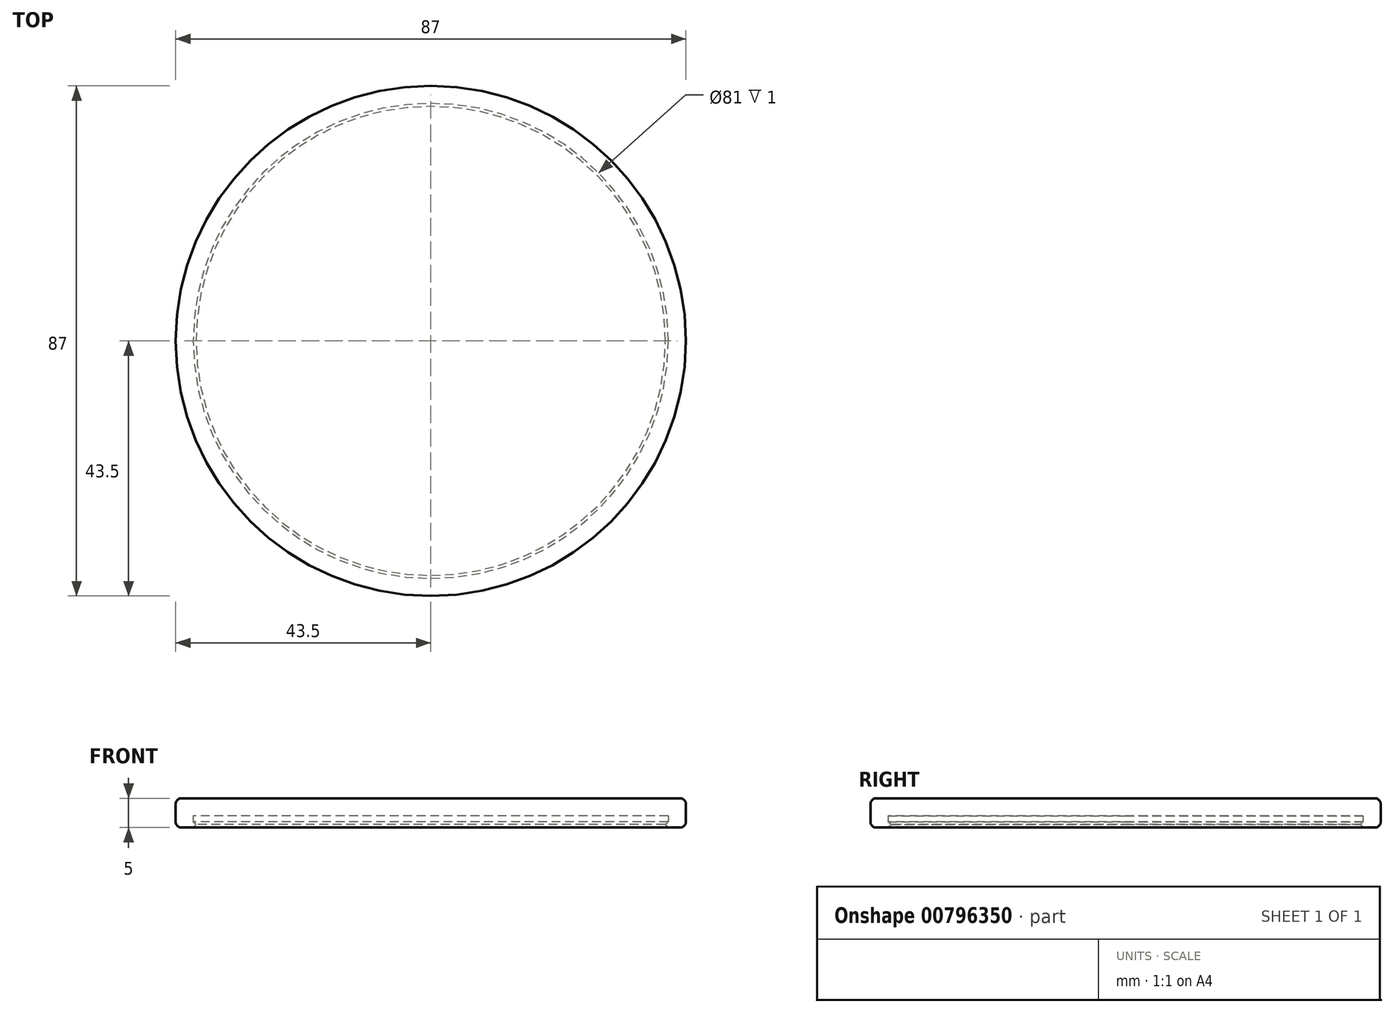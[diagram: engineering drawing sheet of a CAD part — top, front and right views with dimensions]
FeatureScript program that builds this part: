
annotation { "Feature Type Name" : "Feature", "Feature Type Description" : "" }
export const myFeature = defineFeature(function(context is Context, id is Id, definition is map)
    precondition{}
    {
        {
            var Q0;
            Q0=qCreatedBy(makeId("Top.planeOp"),FACE);
            var sketch = newSketch(context, id + "F0", { "sketchPlane" : qUnion([Q0])});
            skCircle(sketch, "E0", {"center": v(0, 0) * mm, "radius": 40.5 * mm});
            skCircle(sketch, "E1", {"center": v(0, 0) * mm, "radius": 43.5 * mm});
            skSolve(sketch);
        }
        {
            var Q0;
            Q0=makeQuery(id+"F0.imprint","IMPRINT",FACE,{"disambiguationData":[TD([[makeQuery(id+"F0.imprint","IMPRINT",EDGE,{"derivedFrom":sQuery(id+"F0.wireOp",EDGE,"E0")}),-1.0]])]});
            extrude(context, id + "F1", {"entities" : qUnion([Q0]), "depth" : 2 * mm, "offsetDistance" : 25 * mm});
        }
        {
            var Q0;
            Q0=makeQuery(id+"F1.opExtrude","CAP_FACE",FACE,{"disambiguationData":[OSD([sQuery(id+"F0.wireOp",EDGE,"E0"),sQuery(id+"F0.wireOp",EDGE,"E1")])],"isStart":false});
            var sketch = newSketch(context, id + "F2", { "sketchPlane" : qUnion([Q0])});
            skCircle(sketch, "E2.0", {"center": v(0, 0) * mm, "radius": 43.5 * mm});
            skSolve(sketch);
        }
        {
            var Q0;
            Q0 = qSketchRegion(id + "F2", true);
            extrude(context, id + "F3", {"entities" : qUnion([Q0]), "operationType" : NewBodyOperationType.ADD, "depth" : 3 * mm, "offsetDistance" : 25 * mm});
        }
        {
            var Q0;
            Q0=qCreatedBy(makeId("Front.planeOp"),FACE);
            var sketch = newSketch(context, id + "F4", { "sketchPlane" : qUnion([Q0])});
            skLineSegment(sketch, "E3.0", {"start": v(-40.5, 2) * mm, "end": v(40.5, 2) * mm, "construction": true});
            skLineSegment(sketch, "E4.0", {"start": v(-43.5, 0) * mm, "end": v(43.5, 0) * mm, "construction": true});
            skLineSegment(sketch, "E5", {"start": v(40.5, 0) * mm, "end": v(40, 0.5) * mm});
            skLineSegment(sketch, "E6", {"start": v(40, 0.5) * mm, "end": v(40.5, 1) * mm});
            skLineSegment(sketch, "E7", {"start": v(40.5, 1) * mm, "end": v(40.5, 0) * mm});
            skLineSegment(sketch, "E8", {"start": v(0, 0) * mm, "end": v(0, -7.02) * mm, "construction": true});
            skSolve(sketch);
        }
        {
            var Q0;
            Q0 = qSketchRegion(id + "F4", true);
            var Q1;
            Q1=sQuery(id+"F4.wireOp",EDGE,"E8");
            revolve(context, id + "F5", {"operationType" : NewBodyOperationType.ADD, "surfaceOperationType" : NewSurfaceOperationType.NEW, "entities" : qUnion([Q0]), "axis" : qUnion([Q1]), "revolveType" : RevolveType.FULL});
        }
        {
            var Q0;
            Q0=makeQuery(id+"F3.opExtrude","CAP_EDGE",EDGE,{"disambiguationData":[OSD([sQuery(id+"F2.wireOp",EDGE,"E2.0")])],"isStart":false});
            var Q1;
            Q1=makeQuery(id+"F1.opExtrude","CAP_EDGE",EDGE,{"disambiguationData":[OSD([sQuery(id+"F0.wireOp",EDGE,"E1")])],"isStart":true});
            fillet(context, id + "F6", {"entities" : qUnion([Q0, Q1]), "radius" : 1 * mm, "tangentPropagation" : true, "allowEdgeOverflow" : false});
        }
    });
